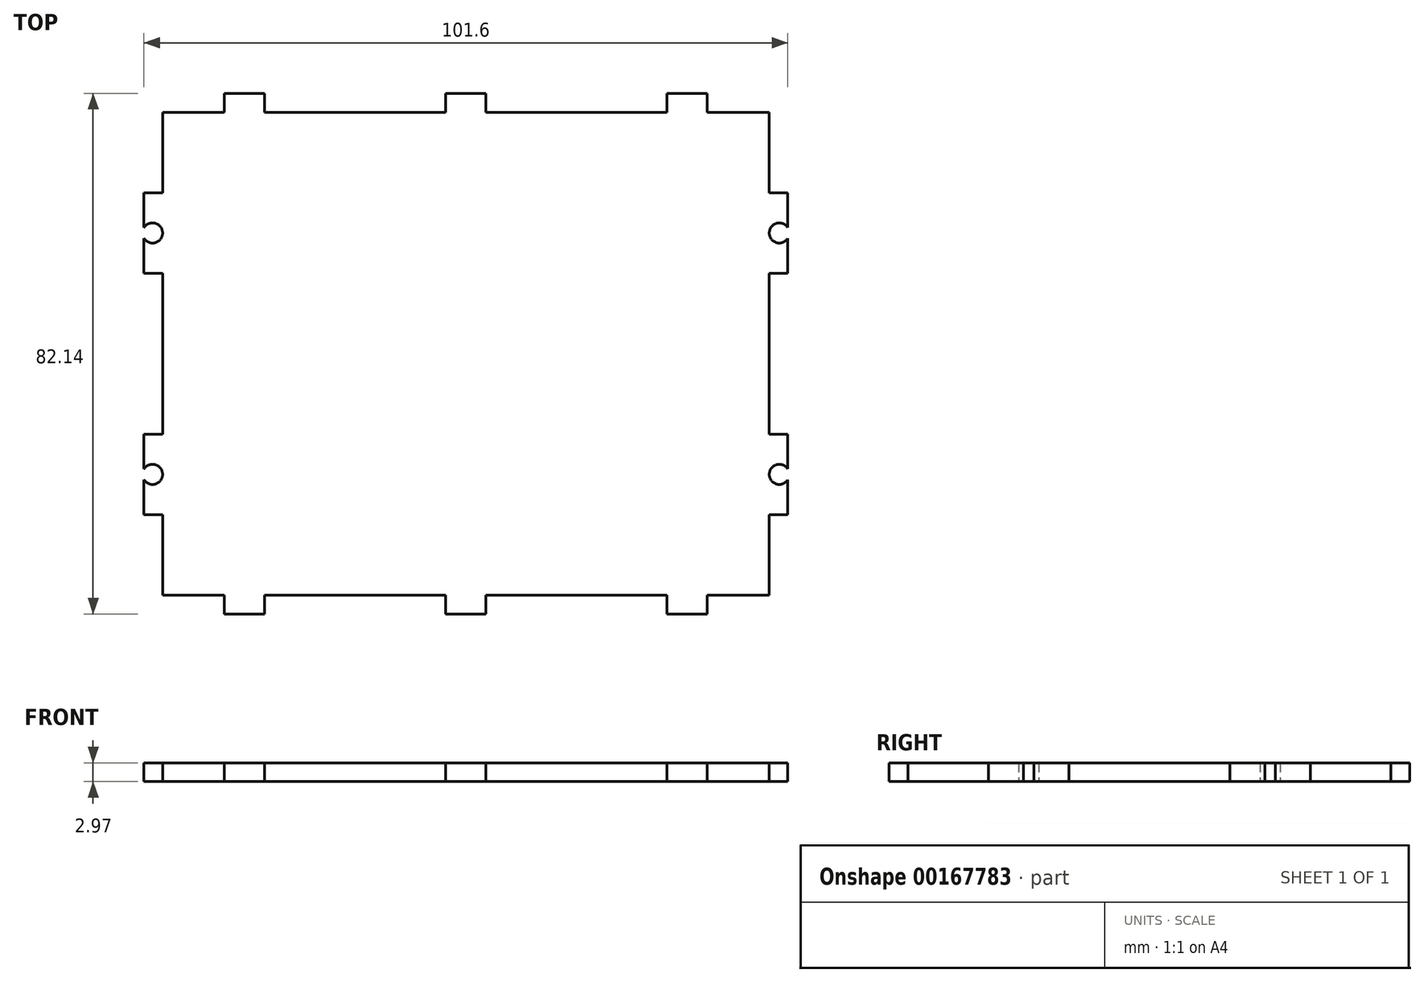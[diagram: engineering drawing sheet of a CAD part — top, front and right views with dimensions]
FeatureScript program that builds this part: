
annotation { "Feature Type Name" : "Feature", "Feature Type Description" : "" }
export const myFeature = defineFeature(function(context is Context, id is Id, definition is map)
    precondition{}
    {
        {
            var Q0;
            Q0=qCreatedBy(makeId("Top.planeOp"),FACE);
            var sketch = newSketch(context, id + "F0", { "sketchPlane" : qUnion([Q0])});
            skLineSegment(sketch, "E0.bottom", {"start": v(47.83, 38.1) * mm, "end": v(38.1, 38.1) * mm});
            skLineSegment(sketch, "E0.top", {"start": v(47.83, -38.1) * mm, "end": v(38.1, -38.1) * mm});
            skLineSegment(sketch, "E0.left", {"start": v(50.8, 25.4) * mm, "end": v(50.8, 19.9) * mm});
            skLineSegment(sketch, "E0.right", {"start": v(-50.8, 25.4) * mm, "end": v(-50.8, 19.9) * mm});
            skPoint(sketch, "E0.middle", {"position": v(0, 0) * mm});
            skLineSegment(sketch, "E1", {"start": v(-50.8, 0) * mm, "end": v(47.83, 0) * mm, "construction": true});
            skArc(sketch, "E2", {"start": v(-50.8, 18.2) * mm, "mid": v(-47.87, 19.05) * mm, "end": v(-50.8, 19.9) * mm});
            skLineSegment(sketch, "E3", {"start": v(0, 38.1) * mm, "end": v(0, -38.1) * mm, "construction": true});
            skArc(sketch, "E4.MirrorC", {"start": v(50.8, 18.2) * mm, "mid": v(47.87, 19.05) * mm, "end": v(50.8, 19.9) * mm});
            skArc(sketch, "E5.MirrorC", {"start": v(-50.8, -18.2) * mm, "mid": v(-47.87, -19.05) * mm, "end": v(-50.8, -19.9) * mm});
            skArc(sketch, "E6.MirrorC", {"start": v(50.8, -18.2) * mm, "mid": v(47.87, -19.05) * mm, "end": v(50.8, -19.9) * mm});
            skLineSegment(sketch, "E7.top", {"start": v(-38.1, -41.07) * mm, "end": v(-31.75, -41.07) * mm});
            skLineSegment(sketch, "E7.left", {"start": v(-38.1, -38.1) * mm, "end": v(-38.1, -41.07) * mm});
            skLineSegment(sketch, "E7.right", {"start": v(-31.75, -38.1) * mm, "end": v(-31.75, -41.07) * mm});
            skLineSegment(sketch, "E8.MirrorCS", {"start": v(38.1, -41.07) * mm, "end": v(31.75, -41.07) * mm});
            skLineSegment(sketch, "E9.MirrorCS", {"start": v(31.75, -38.1) * mm, "end": v(31.75, -41.07) * mm});
            skLineSegment(sketch, "E10.MirrorCS", {"start": v(38.1, -38.1) * mm, "end": v(38.1, -41.07) * mm});
            skLineSegment(sketch, "E11.MirrorCS", {"start": v(-38.1, 41.07) * mm, "end": v(-31.75, 41.07) * mm});
            skLineSegment(sketch, "E12.MirrorCS", {"start": v(-38.1, 38.1) * mm, "end": v(-38.1, 41.07) * mm});
            skLineSegment(sketch, "E13.MirrorCS", {"start": v(-31.75, 38.1) * mm, "end": v(-31.75, 41.07) * mm});
            skLineSegment(sketch, "E14.MirrorCS", {"start": v(31.75, 38.1) * mm, "end": v(31.75, 41.07) * mm});
            skLineSegment(sketch, "E15.MirrorCS", {"start": v(38.1, 41.07) * mm, "end": v(31.75, 41.07) * mm});
            skLineSegment(sketch, "E16.MirrorCS", {"start": v(38.1, 38.1) * mm, "end": v(38.1, 41.07) * mm});
            skLineSegment(sketch, "E17.top", {"start": v(-3.18, -41.07) * mm, "end": v(3.17, -41.07) * mm});
            skLineSegment(sketch, "E17.left", {"start": v(-3.18, -38.1) * mm, "end": v(-3.18, -41.07) * mm});
            skLineSegment(sketch, "E17.right", {"start": v(3.17, -38.1) * mm, "end": v(3.17, -41.07) * mm});
            skLineSegment(sketch, "E18.MirrorCS", {"start": v(3.17, 38.1) * mm, "end": v(3.17, 41.07) * mm});
            skLineSegment(sketch, "E19.MirrorCS", {"start": v(-3.18, 41.07) * mm, "end": v(3.17, 41.07) * mm});
            skLineSegment(sketch, "E20.MirrorCS", {"start": v(-3.18, 38.1) * mm, "end": v(-3.18, 41.07) * mm});
            skLineSegment(sketch, "E21.trimOffspring", {"start": v(-50.8, -19.9) * mm, "end": v(-50.8, -25.4) * mm});
            skLineSegment(sketch, "E22.trimOffspring", {"start": v(-50.8, 18.2) * mm, "end": v(-50.8, 12.7) * mm});
            skLineSegment(sketch, "E23.trimOffspring", {"start": v(50.8, 18.2) * mm, "end": v(50.8, 12.7) * mm});
            skLineSegment(sketch, "E24.trimOffspring", {"start": v(50.8, -19.9) * mm, "end": v(50.8, -25.4) * mm});
            skLineSegment(sketch, "E25.bottom", {"start": v(-50.8, 25.4) * mm, "end": v(-47.83, 25.4) * mm});
            skLineSegment(sketch, "E25.top", {"start": v(-50.8, 12.7) * mm, "end": v(-47.83, 12.7) * mm});
            skLineSegment(sketch, "E26", {"start": v(-47.83, 25.4) * mm, "end": v(-47.83, 38.1) * mm});
            skLineSegment(sketch, "E27", {"start": v(-47.83, 12.7) * mm, "end": v(-47.83, 0) * mm});
            skLineSegment(sketch, "E28.MirrorCS", {"start": v(-47.83, -12.7) * mm, "end": v(-47.83, 0) * mm});
            skLineSegment(sketch, "E29.MirrorCS", {"start": v(-50.8, -12.7) * mm, "end": v(-47.83, -12.7) * mm});
            skLineSegment(sketch, "E30.MirrorCS", {"start": v(-47.83, -25.4) * mm, "end": v(-47.83, -38.1) * mm});
            skLineSegment(sketch, "E31.MirrorCS", {"start": v(-50.8, -25.4) * mm, "end": v(-47.83, -25.4) * mm});
            skLineSegment(sketch, "E32.trimOffspring", {"start": v(-50.8, -12.7) * mm, "end": v(-50.8, -18.2) * mm});
            skPoint(sketch, "E33.orphan", {"position": v(-50.8, -38.1) * mm});
            skPoint(sketch, "E34.orphan", {"position": v(-50.8, 38.1) * mm});
            skLineSegment(sketch, "E35.MirrorCS", {"start": v(47.83, 12.7) * mm, "end": v(47.83, 0) * mm});
            skLineSegment(sketch, "E36.MirrorCS", {"start": v(47.83, -12.7) * mm, "end": v(47.83, 0) * mm});
            skLineSegment(sketch, "E37.MirrorCS", {"start": v(50.8, -12.7) * mm, "end": v(47.83, -12.7) * mm});
            skLineSegment(sketch, "E38.MirrorCS", {"start": v(50.8, -25.4) * mm, "end": v(47.83, -25.4) * mm});
            skLineSegment(sketch, "E39.MirrorCS", {"start": v(50.8, 12.7) * mm, "end": v(47.83, 12.7) * mm});
            skLineSegment(sketch, "E40.MirrorCS", {"start": v(47.83, -25.4) * mm, "end": v(47.83, -38.1) * mm});
            skLineSegment(sketch, "E41.MirrorCS", {"start": v(47.83, 25.4) * mm, "end": v(47.83, 38.1) * mm});
            skLineSegment(sketch, "E42.MirrorCS", {"start": v(50.8, 25.4) * mm, "end": v(47.83, 25.4) * mm});
            skPoint(sketch, "E43.orphan", {"position": v(50.8, 38.1) * mm});
            skLineSegment(sketch, "E44.trimOffspring", {"start": v(50.8, -12.7) * mm, "end": v(50.8, -18.2) * mm});
            skPoint(sketch, "E45.orphan", {"position": v(50.8, -38.1) * mm});
            skLineSegment(sketch, "E46.trimOffspring", {"start": v(-38.1, 38.1) * mm, "end": v(-47.83, 38.1) * mm});
            skLineSegment(sketch, "E47.trimOffspring", {"start": v(-3.18, 38.1) * mm, "end": v(-31.75, 38.1) * mm});
            skLineSegment(sketch, "E48.trimOffspring", {"start": v(31.75, 38.1) * mm, "end": v(3.18, 38.1) * mm});
            skPoint(sketch, "E49.MirrorCS.end.orphan", {"position": v(47.83, 12.7) * mm});
            skPoint(sketch, "E49.MirrorCS.start.orphan", {"position": v(47.83, 25.4) * mm});
            skPoint(sketch, "E50.MirrorCS.end.orphan", {"position": v(47.83, -12.7) * mm});
            skPoint(sketch, "E50.MirrorCS.start.orphan", {"position": v(47.83, -25.4) * mm});
            skPoint(sketch, "E51.orphan", {"position": v(50.8, 0) * mm});
            skLineSegment(sketch, "E52.trimOffspring", {"start": v(31.75, -38.1) * mm, "end": v(3.18, -38.1) * mm});
            skPoint(sketch, "E53.MirrorCS.end.orphan", {"position": v(-47.83, -12.7) * mm});
            skPoint(sketch, "E53.MirrorCS.start.orphan", {"position": v(-47.83, -25.4) * mm});
            skLineSegment(sketch, "E54.trimOffspring", {"start": v(-3.18, -38.1) * mm, "end": v(-31.75, -38.1) * mm});
            skLineSegment(sketch, "E55.trimOffspring", {"start": v(-38.1, -38.1) * mm, "end": v(-47.83, -38.1) * mm});
            skSolve(sketch);
        }
        {
            var Q0;
            Q0 = qSketchRegion(id + "F0", true);
            extrude(context, id + "F1", {"entities" : qUnion([Q0]), "depth" : 2.97 * mm});
        }
    });
